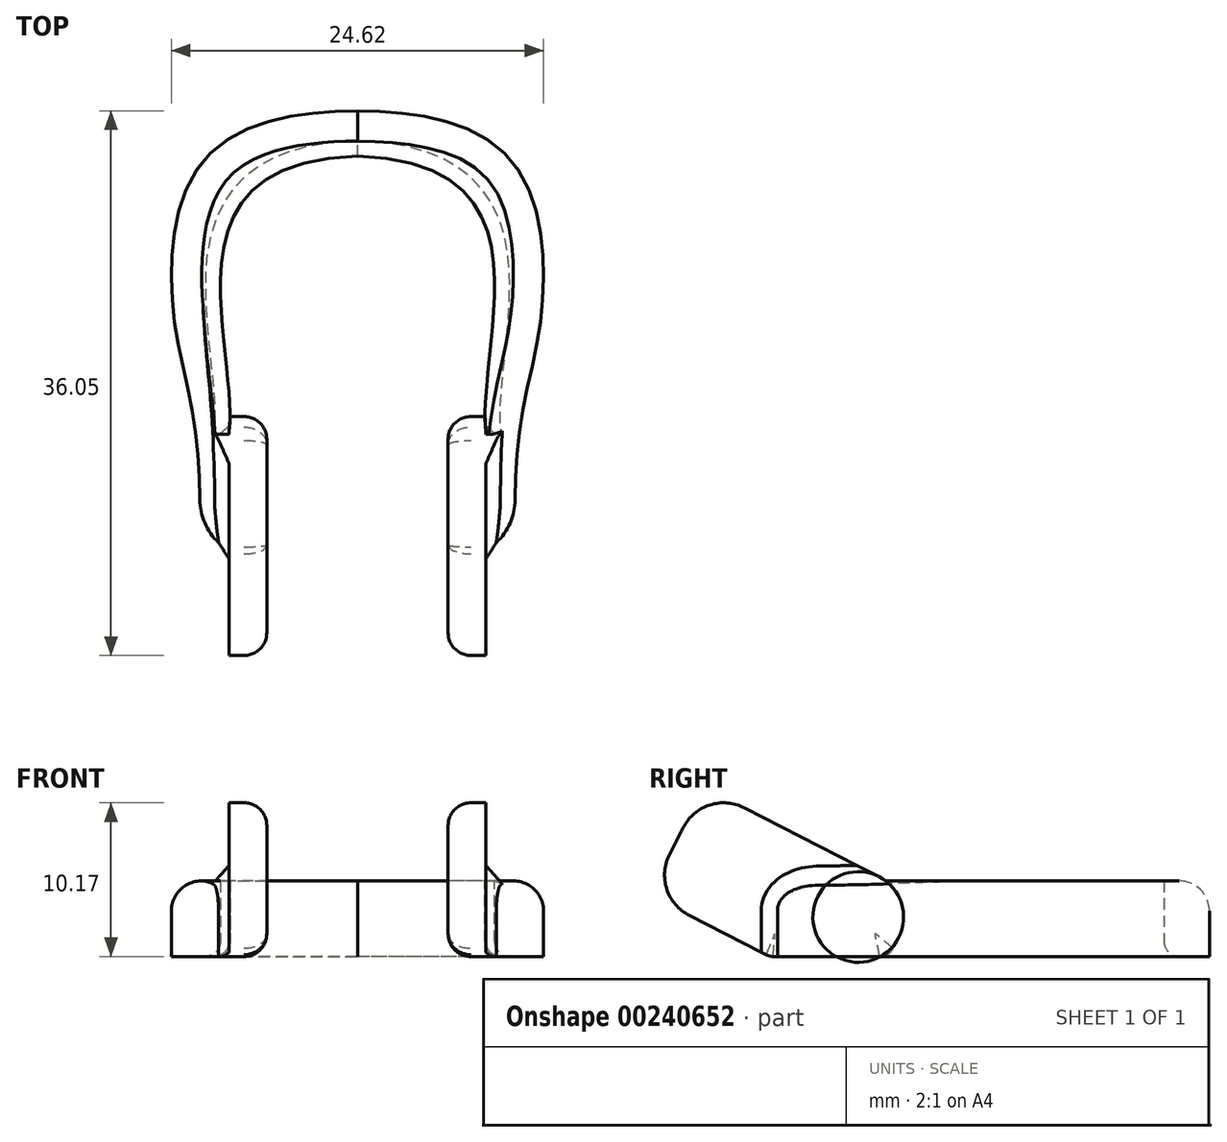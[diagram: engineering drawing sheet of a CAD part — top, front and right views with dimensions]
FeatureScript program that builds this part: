
annotation { "Feature Type Name" : "Feature", "Feature Type Description" : "" }
export const myFeature = defineFeature(function(context is Context, id is Id, definition is map)
    precondition{}
    {
        {
            var Q0;
            Q0=qCreatedBy(makeId("Right.planeOp"),FACE);
            cPlane(context, id + "F0", {"entities" : qUnion([Q0]), "cplaneType" : CPlaneType.OFFSET, "offset" : 6 * mm, "width" : 150 * mm, "height" : 150 * mm});
        }
        {
            var Q0;
            Q0=qCreatedBy(id+"F0.planeOp",FACE);
            var sketch = newSketch(context, id + "F1", { "sketchPlane" : qUnion([Q0])});
            skLineSegment(sketch, "E0.bottom", {"start": v(-13.94, 4.09) * mm, "end": v(-5.96, 0) * mm});
            skLineSegment(sketch, "E0.top", {"start": v(-10.3, 11.2) * mm, "end": v(3.94, 3.91) * mm});
            skLineSegment(sketch, "E0.left", {"start": v(-13.94, 4.09) * mm, "end": v(-10.3, 11.2) * mm});
            skLineSegment(sketch, "E0.right", {"start": v(1.94, 0) * mm, "end": v(3.94, 3.91) * mm});
            skPoint(sketch, "E0.middle", {"position": v(-5, 4) * mm});
            skLineSegment(sketch, "E1", {"start": v(-5.96, 0) * mm, "end": v(1.94, 0) * mm});
            skPoint(sketch, "E2.orphan", {"position": v(0.3, -3.2) * mm});
            skSolve(sketch);
        }
        {
            var Q0;
            Q0 = qSketchRegion(id + "F1", true);
            extrude(context, id + "F2", {"entities" : qUnion([Q0]), "depth" : 2.5 * mm, "offsetDistance" : 25 * mm});
        }
        {
            var Q0;
            Q0=makeQuery(id+"F2.opExtrude","SWEPT_EDGE",EDGE,{"disambiguationData":[OSD([sQuery(id+"F1.wireOp",EDGE,"E0.top"),sQuery(id+"F1.wireOp",EDGE,"E0.left")])]});
            var Q1;
            Q1=makeQuery(id+"F2.opExtrude","SWEPT_EDGE",EDGE,{"disambiguationData":[OSD([sQuery(id+"F1.wireOp",EDGE,"E0.bottom"),sQuery(id+"F1.wireOp",EDGE,"E0.left")])]});
            var Q2;
            Q2=makeQuery(id+"F2.opExtrude","SWEPT_EDGE",EDGE,{"disambiguationData":[OSD([sQuery(id+"F1.wireOp",EDGE,"E0.top"),sQuery(id+"F1.wireOp",EDGE,"E0.right")])]});
            fillet(context, id + "F3", {"entities" : qUnion([Q0, Q1, Q2]), "tangentPropagation" : true, "radius" : 3 * mm, "defaultsChanged" : false, "vertexSettings" : [], "allowEdgeOverflow" : false});
        }
        {
            var Q0;
            Q0=makeQuery(id+"F2.opExtrude","CAP_FACE",FACE,{"disambiguationData":[OSD([sQuery(id+"F1.wireOp",EDGE,"E0.bottom"),sQuery(id+"F1.wireOp",EDGE,"E0.top"),sQuery(id+"F1.wireOp",EDGE,"E0.left"),sQuery(id+"F1.wireOp",EDGE,"E0.right")])],"isStart":true});
            fillet(context, id + "F4", {"entities" : qUnion([Q0]), "tangentPropagation" : true, "radius" : 1.5 * mm, "defaultsChanged" : true, "vertexSettings" : [], "allowEdgeOverflow" : false});
        }
        {
            var Q0;
            Q0=qCreatedBy(makeId("Top.planeOp"),FACE);
            var sketch = newSketch(context, id + "F5", { "sketchPlane" : qUnion([Q0])});
            skPoint(sketch, "E3.0", {"position": v(8.5, 1.94) * mm});
            skLineSegment(sketch, "E4", {"start": v(8.5, 1.94) * mm, "end": v(8.5, -5.96) * mm});
            skLineSegment(sketch, "E5", {"start": v(8.5, -5.96) * mm, "end": v(10.5, -5.96) * mm});
            skFitSpline(sketch, "E6", {"points": [v(10.5, -5.96) * mm, v(12.02, 8.57) * mm, v(11.07, 18.51) * mm, v(0, 23.14) * mm], "startDerivative": vector(-3.34, 67.62) * mm, "endDerivative": vector(-56.04, 0.4) * mm});
            skFitSpline(sketch, "E7", {"points": [v(8.5, 1.94) * mm, v(9, 9.76) * mm, v(0, 20.14) * mm], "startDerivative": vector(-1.74, 13) * mm, "endDerivative": vector(-47.57, 1.1) * mm});
            skFitSpline(sketch, "E8.MirrorCS", {"points": [v(-10.5, -5.96) * mm, v(-12.02, 8.57) * mm, v(-11.07, 18.51) * mm, v(0, 23.14) * mm], "startDerivative": vector(3.34, 67.62) * mm, "endDerivative": vector(56.04, 0.4) * mm});
            skLineSegment(sketch, "E9.MirrorCS", {"start": v(-8.5, 1.94) * mm, "end": v(-8.5, -5.96) * mm});
            skLineSegment(sketch, "E10.MirrorCS", {"start": v(-8.5, -5.96) * mm, "end": v(-10.5, -5.96) * mm});
            skFitSpline(sketch, "E11.MirrorCS", {"points": [v(-8.5, 1.94) * mm, v(-9, 9.76) * mm, v(0, 20.14) * mm], "startDerivative": vector(1.74, 13) * mm, "endDerivative": vector(47.57, 1.1) * mm});
            skSolve(sketch);
        }
        {
            var Q0;
            Q0 = qSketchRegion(id + "F5", true);
            extrude(context, id + "F6", {"entities" : qUnion([Q0]), "depth" : 5 * mm, "offsetDistance" : 25 * mm});
        }
        {
            var Q0;
            Q0=makeQuery(id+"F2.opExtrude","SWEPT_BODY",BODY,{"disambiguationData":[OSD([sQuery(id+"F1.wireOp",EDGE,"E0.bottom"),sQuery(id+"F1.wireOp",EDGE,"E0.top"),sQuery(id+"F1.wireOp",EDGE,"E0.left"),sQuery(id+"F1.wireOp",EDGE,"E0.right")])]});
            var Q1;
            Q1=qCreatedBy(makeId("Right.planeOp"),FACE);
            mirror(context, id + "F7", {"operationType" : NewBodyOperationType.ADD, "entities" : qUnion([Q0]), "mirrorPlane" : qUnion([Q1])});
        }
        {
            var Q0;
            Q0=makeQuery(id+"F6.opExtrude","SWEPT_EDGE",EDGE,{"disambiguationData":[OSD([sQuery(id+"F5.wireOp",EDGE,"E5"),sQuery(id+"F5.wireOp",EDGE,"E6")])]});
            var Q1;
            Q1=makeQuery(id+"F6.opExtrude","SWEPT_EDGE",EDGE,{"disambiguationData":[OSD([sQuery(id+"F5.wireOp",EDGE,"E8.MirrorCS"),sQuery(id+"F5.wireOp",EDGE,"E10.MirrorCS")])]});
            fillet(context, id + "F8", {"entities" : qUnion([Q0, Q1]), "tangentPropagation" : true, "radius" : 4 * mm, "defaultsChanged" : false, "vertexSettings" : [], "allowEdgeOverflow" : false});
        }
        {
            var Q0;
            Q0=makeQuery(id+"F6.opExtrude","CAP_EDGE",EDGE,{"disambiguationData":[OSD([sQuery(id+"F5.wireOp",EDGE,"E6")])],"isStart":false});
            var Q1;
            Q1=makeQuery(id+"F6.opExtrude","CAP_EDGE",EDGE,{"disambiguationData":[OSD([sQuery(id+"F5.wireOp",EDGE,"E8.MirrorCS")])],"isStart":false});
            fillet(context, id + "F9", {"entities" : qUnion([Q0, Q1]), "tangentPropagation" : true, "radius" : 2 * mm, "defaultsChanged" : false, "vertexSettings" : [], "allowEdgeOverflow" : false});
        }
        {
            var Q0;
            Q0=makeQuery(id+"F9.opFillet","BLEND_EDGE",EDGE,{"blendedFrom":[makeQuery(id+"F6.opExtrude","CAP_EDGE",EDGE,{"disambiguationData":[OSD([sQuery(id+"F5.wireOp",EDGE,"E6")])],"isStart":false}),makeQuery(id+"F2.opExtrude","CAP_FACE",FACE,{"disambiguationData":[OSD([sQuery(id+"F1.wireOp",EDGE,"E0.bottom"),sQuery(id+"F1.wireOp",EDGE,"E0.top"),sQuery(id+"F1.wireOp",EDGE,"E0.left"),sQuery(id+"F1.wireOp",EDGE,"E0.right"),sQuery(id+"F1.wireOp",EDGE,"E1")])],"isStart":false})],"blendedInto":[makeQuery(id+"F2.opExtrude","CAP_FACE",FACE,{"disambiguationData":[OSD([sQuery(id+"F1.wireOp",EDGE,"E0.bottom"),sQuery(id+"F1.wireOp",EDGE,"E0.top"),sQuery(id+"F1.wireOp",EDGE,"E0.left"),sQuery(id+"F1.wireOp",EDGE,"E0.right"),sQuery(id+"F1.wireOp",EDGE,"E1")])],"isStart":false})]});
            var Q1;
            Q1=makeQuery(id+"F9.opFillet","BLEND_EDGE",EDGE,{"blendedFrom":[makeQuery(id+"F6.opExtrude","CAP_EDGE",EDGE,{"disambiguationData":[OSD([sQuery(id+"F5.wireOp",EDGE,"E8.MirrorCS")])],"isStart":false}),makeQuery(id+"F7.opPattern","COPY",FACE,{"derivedFrom":makeQuery(id+"F2.opExtrude","CAP_FACE",FACE,{"disambiguationData":[OSD([sQuery(id+"F1.wireOp",EDGE,"E0.bottom"),sQuery(id+"F1.wireOp",EDGE,"E0.top"),sQuery(id+"F1.wireOp",EDGE,"E0.left"),sQuery(id+"F1.wireOp",EDGE,"E0.right"),sQuery(id+"F1.wireOp",EDGE,"E1")])],"isStart":false}),"instanceName":"1"})],"blendedInto":[makeQuery(id+"F7.opPattern","COPY",FACE,{"derivedFrom":makeQuery(id+"F2.opExtrude","CAP_FACE",FACE,{"disambiguationData":[OSD([sQuery(id+"F1.wireOp",EDGE,"E0.bottom"),sQuery(id+"F1.wireOp",EDGE,"E0.top"),sQuery(id+"F1.wireOp",EDGE,"E0.left"),sQuery(id+"F1.wireOp",EDGE,"E0.right"),sQuery(id+"F1.wireOp",EDGE,"E1")])],"isStart":false}),"instanceName":"1"})]});
            chamfer(context, id + "F10", {"entities" : qUnion([Q0, Q1]), "width" : 1 * mm, "tangentPropagation" : true});
        }
        {
            var Q0;
            Q0=makeQuery(id+"F7.opPattern","COPY",EDGE,{"derivedFrom":makeQuery(id+"F2.opExtrude","SWEPT_EDGE",EDGE,{"disambiguationData":[OSD([sQuery(id+"F1.wireOp",EDGE,"E0.right"),sQuery(id+"F1.wireOp",EDGE,"E1")])]}),"instanceName":"1"});
            var Q1;
            Q1=makeQuery(id+"F2.opExtrude","SWEPT_EDGE",EDGE,{"disambiguationData":[OSD([sQuery(id+"F1.wireOp",EDGE,"E0.right"),sQuery(id+"F1.wireOp",EDGE,"E1")])]});
            var Q2;
            Q2=makeQuery(id+"F2.opExtrude","SWEPT_EDGE",EDGE,{"disambiguationData":[OSD([sQuery(id+"F1.wireOp",EDGE,"E0.bottom"),sQuery(id+"F1.wireOp",EDGE,"E1")])]});
            var Q3;
            Q3=makeQuery(id+"F7.opPattern","COPY",EDGE,{"derivedFrom":makeQuery(id+"F2.opExtrude","SWEPT_EDGE",EDGE,{"disambiguationData":[OSD([sQuery(id+"F1.wireOp",EDGE,"E0.bottom"),sQuery(id+"F1.wireOp",EDGE,"E1")])]}),"instanceName":"1"});
            var Q4;
            Q4=makeQuery(id+"F6.opExtrude","CAP_EDGE",EDGE,{"disambiguationData":[OSD([sQuery(id+"F5.wireOp",EDGE,"E7")])],"isStart":true});
            var Q5;
            Q5=makeQuery(id+"F6.opExtrude","CAP_EDGE",EDGE,{"disambiguationData":[OSD([sQuery(id+"F5.wireOp",EDGE,"E11.MirrorCS")])],"isStart":true});
            fillet(context, id + "F11", {"entities" : qUnion([Q0, Q1, Q2, Q3, Q4, Q5]), "tangentPropagation" : true, "radius" : 1 * mm, "defaultsChanged" : false, "vertexSettings" : [], "allowEdgeOverflow" : false});
        }
    });
